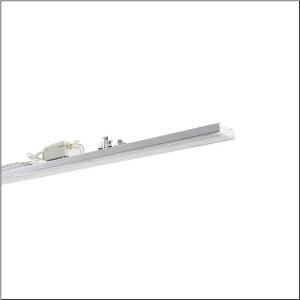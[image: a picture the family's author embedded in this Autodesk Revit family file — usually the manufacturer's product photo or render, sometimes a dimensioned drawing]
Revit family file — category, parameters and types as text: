
# Revit family: licross_21_recessed_mo_52tl18de445g
name_source: partatom
category: Lighting Fixtures
units: mm (PartAtom-declared; Revit-internal decimal feet)

## family parameters
Cut with Voids When Loaded = No
Host = Face
Light Source = No
Part Type = Normal
Room Calculation Point = No
Round Connector Dimension = Use Diameter
Shared = No

## types (1)
- --- (1 x LED, 4990 lm, 29.9 W, 4000K)
    Apparent Load = 30 VA
    CIE Flux Codes = 79 95 99 100 100
    Color Rendering = 80
    Color Temperature = 4000K
    Default Elevation = 1800 mm
    Description = Licross 21 Recessed MO, luminaire insert, of sheet steel, galvanised, coil coated, white, length: 750mm, width: 66mm, height: 67mm, LED rated luminous flux: 4.990lm, light colour: 840, SDCM (Standard Deviation of Colour Matching)MacAdam ≤ 3 SDCM (initial), control gear: DALI 2, with plug, 5-pole, with phase selection, mains connection: 220..240V, AC, 50/60Hz, rated input power: 30W, internal wiring halogen-free, primary light control with lens, of plastic, primary optical cover: cover, of PMMA, light emission: direct distribution, primary light characteristic: symmetric, protection rating (complete): IP40, insulation class (complete): insulation class I (protective earthing), certification: CE, ENEC, VDE, UKCA, protection symbol: D if used in an environment without relevant dust loads with corresponding accessories, impact resistance: IK06, permissible ambient temperature for indoor applications: -25..+35°C, corresponds to IFS (International Featured Standards) requirements for safety and quality in the food industry, reducing of maximum allowable ambient temperature of 5°C with ceiling mounting, LABS conformity tested according to VDMA 24364:2018-05, The light source and the operating device comply with the requirements of the Ecodesign Regulation (EU) 2019/2020 and are replaceable in accordance with this regulation, packaging unit: 1 piece
    Height = 58 mm
    Lamp = 1 x LED
    Lamp Light Flux = 4990 lm
    Lamp Power = 29.9 W
    Lamp count = 1
    Length = 750 mm
    Luminous efficacy = 167 lm/W
    Manufacturer = Siteco
    ModVariant = No
    Model = 52TL18DE445G
    Mounting Place = Ceiling
    Mounting Type = Pendant
    Number of Poles = 1
    OnlyDefault = Yes
    Power Factor = 1
    Product Name = Licross 21 Recessed MO
    Product group = luminaire insert | ceiling pendant
    ProductGroupID = 901
    Protection Class = Protection class I
    Protection Degree = IP 40
    RLX_Detail_Level = 1
    RLX_Emergency_Light_Flux = 0 lm
    RLX_Emergency_Type = 0
    RLX_Emergency_Type_DB = No
    RlxData = <blob elided: 28977 chars, md5=703b7e5c>
    Socket = socket
    Standby Power = 0 W
    System Light Flux = 4990 lm
    System Power = 30 W
    Type Comments = factory setting: luminous flux: 100 % | dim-lin: 254 | 390 mA
    Type Image = l_1296930.jpg
    URL = http://relux.com
    VarID = @adj_127815
    Voltage = 0 V
    Weight = 0.00 kg
    Width = 66 mm

## geometry (parser evidence)
native form markers: Blend x4, Sweep x8
no freeform markers — native parametric forms only
